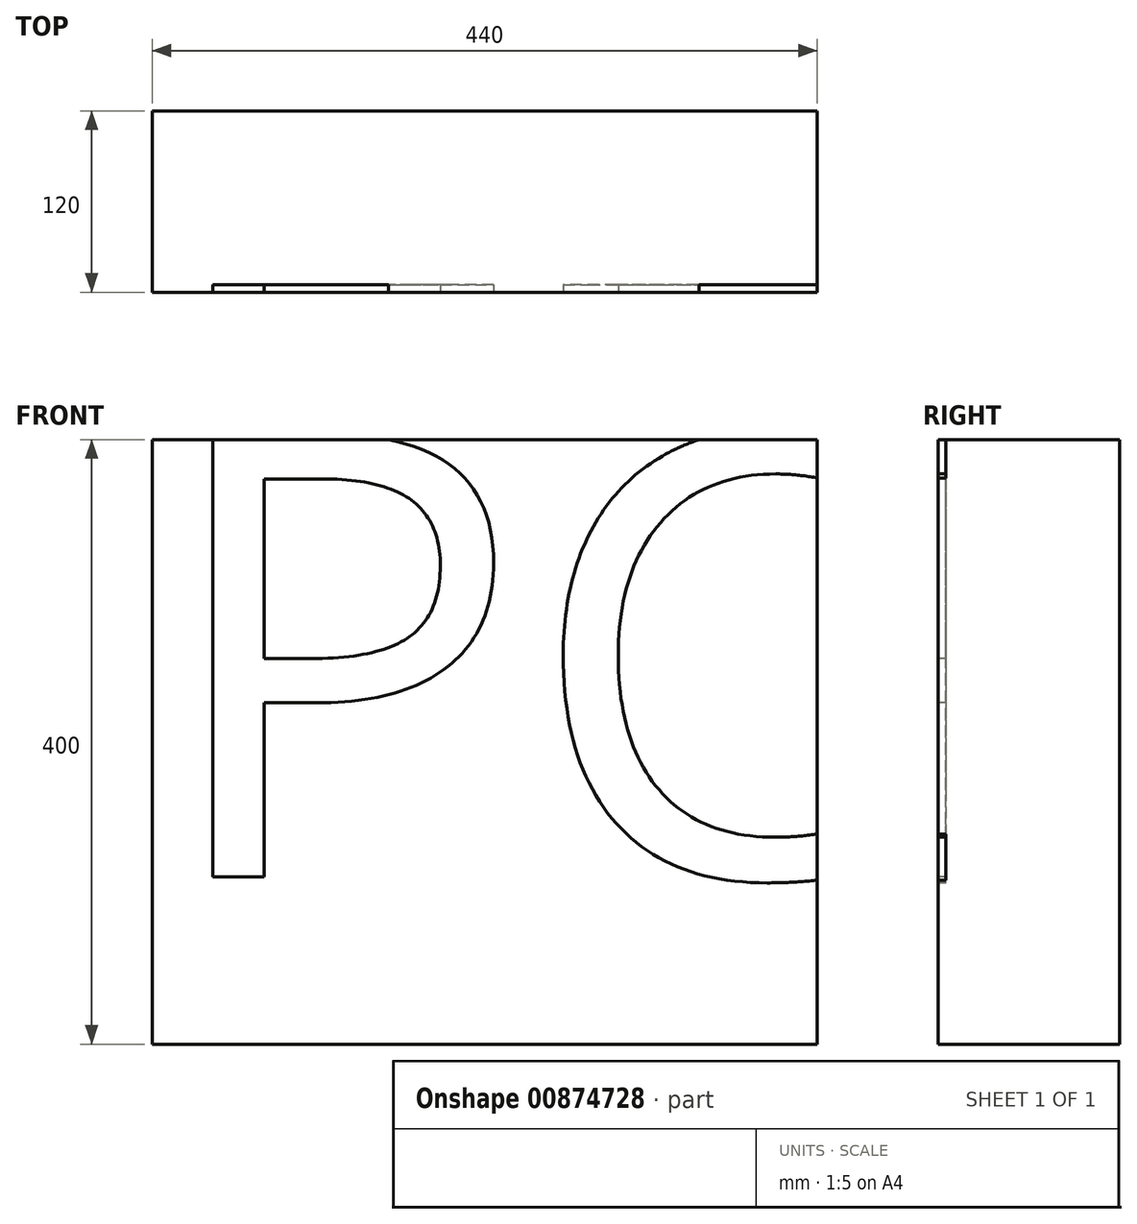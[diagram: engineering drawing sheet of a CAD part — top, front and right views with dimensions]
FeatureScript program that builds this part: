
annotation { "Feature Type Name" : "Feature", "Feature Type Description" : "" }
export const myFeature = defineFeature(function(context is Context, id is Id, definition is map)
    precondition{}
    {
        {
            var Q0;
            Q0=qCreatedBy(makeId("Right.planeOp"),FACE);
            var sketch = newSketch(context, id + "F0", { "sketchPlane" : qUnion([Q0])});
            skLineSegment(sketch, "E0.bottom", {"start": v(39.1, 40.85) * mm, "end": v(159.1, 40.85) * mm});
            skLineSegment(sketch, "E0.top", {"start": v(39.1, 440.85) * mm, "end": v(159.1, 440.85) * mm});
            skLineSegment(sketch, "E0.left", {"start": v(39.1, 40.85) * mm, "end": v(39.1, 440.85) * mm});
            skLineSegment(sketch, "E0.right", {"start": v(159.1, 40.85) * mm, "end": v(159.1, 440.85) * mm});
            skSolve(sketch);
        }
        {
            var Q0;
            Q0=makeQuery(id+"F0.imprint","IMPRINT",FACE,{"disambiguationData":[TD([[makeQuery(id+"F0.imprint","IMPRINT",EDGE,{"derivedFrom":sQuery(id+"F0.wireOp",EDGE,"E0.bottom")}),1.0]])]});
            extrude(context, id + "F1", {"entities" : qUnion([Q0]), "depth" : 440 * mm, "offsetDistance" : 25 * mm});
        }
        {
            var Q0;
            Q0=makeQuery(id+"F1.opExtrude","SWEPT_FACE",FACE,{"disambiguationData":[OSD([sQuery(id+"F0.wireOp",EDGE,"E0.left")])]});
            var sketch = newSketch(context, id + "F2", { "sketchPlane" : qUnion([Q0])});
            skText(sketch, "E1", { "text": "PC", "fontName": "OpenSans-Regular.ttf"});
            const initialGuessF2  = {"E1": [0, 0.15159, 1, 0, 0.29528]};
            skSetInitialGuess(sketch, initialGuessF2);
            skSolve(sketch);
        }
        {
            var Q0;
            Q0 = qSketchRegion(id + "F2", true);
            extrude(context, id + "F3", {"entities" : qUnion([Q0]), "operationType" : NewBodyOperationType.REMOVE, "oppositeDirection" : true, "depth" : 5 * mm, "offsetDistance" : 25 * mm});
        }
    });
